# Revit family: Gira_207000
name_source: partatom
category: Elektroinstallationen
revit_build: Autodesk Revit 2017 (Build: 20160225_1515(x64)
units: mm (PartAtom-declared; Revit-internal decimal feet)

## family parameters
Basisbauteil = Fläche
Beim Laden mit Abzugskörper schneiden = Nein
Bemaßung runder Anschluss = Durchmesser verwenden
Beschriftungsausrichtung beibehalten = Nein
Gemeinsam genutzt = Nein
Raumberechnungspunkt = Nein
Teiletyp = Normal

## types (1)
- Gira_207000
    BIM = https://media.stage.bim.site X1 REG KNX.rfa
    Beschreibung = Gira L1 DRA KNX,Gira L1,,DRA,Features:,- Logic functions:,  A range of functions thanks to the module library with 36 logic modules (e.g. basic mathematical operations, shutters and blind control, temperature control, partition wall control, staircase lighting, random generator).,- Configurable logic nodes (e.g. freely selectable number of inputs).,- Easy parameterisation of timers and scenes:,  up to 20 timers with 10 switching times each.,  up to 20 scene sets with 64 scenes each.,- Up to 480 data points can be used in one project,  (300 KNX group address data points, 180 discretionary device data points).,- Intercom function for exchanging values e. g. between a further L1 or an X1 via Ethernet.,- Optimised start-up:,  Fast project changes and updates during operation without the need to restart the device.,- Two RJ45 sockets with switch functionality support simple loop-through of the patch cable.,- High security:,  Encrypted TLS data transfer between GPA and Gira L1 prevents interception by third parties.,  The device password protects the Gira L1 against unauthorised access.,- Project saving: Saving of a project copy on the Gira L1.,- Start-up:,  The physical address and application are parameterised with the KNX start-up software ETS from version 4.1.8.,  Further configuration is performed in the Gira Project Assistant (GPA). The Gira Project Assistant is available free of charge in the Gira download area.,- Functional extensions and updates via firmware and software updates.,- Hardware prepared for KNX Secure. Future firmware update required.,,Notes :,- Supply via external DC 24 V.
    Bus connection included = Nein
    Bus system KNX = Ja
    Bus system KNX radio = Nein
    Bus system LON = Nein
    Bus system Powernet = Nein
    Bus system radio frequent = Nein
    Central functional unit for senders/actuators = Ja
    Data sheet = https://katalog.gira.de
    Degree of protection (IP) = IP21
    GTIN = 4010337016717
    HAN = 207000
    Hersteller = Gira
    IR sensor = Nein
    Integrated DCF77 receiver = Nein
    Logic object = Ja
    Material = Other
    Material quality = Other
    Mounting method = DRA (DIN-rail adapter)
    Other bus systems = None
    Presence button = Nein
    Productwebsite = http://katalog.gira.de
    Status-LED = Ja
    Surface finishing = Not applicable
    Surface protection = Other
    Temperature controller = Ja
    Transparent = Nein
    Typname = Gira L1 KNX DRA
    URL = https://www.gira.de
    Vorgabe-Ansicht = 1219 mm
    With anti-theft/dismantling protection = Ja
    With display = Ja

## geometry (parser evidence)
native form markers: Sweep x2
no freeform markers — native parametric forms only
